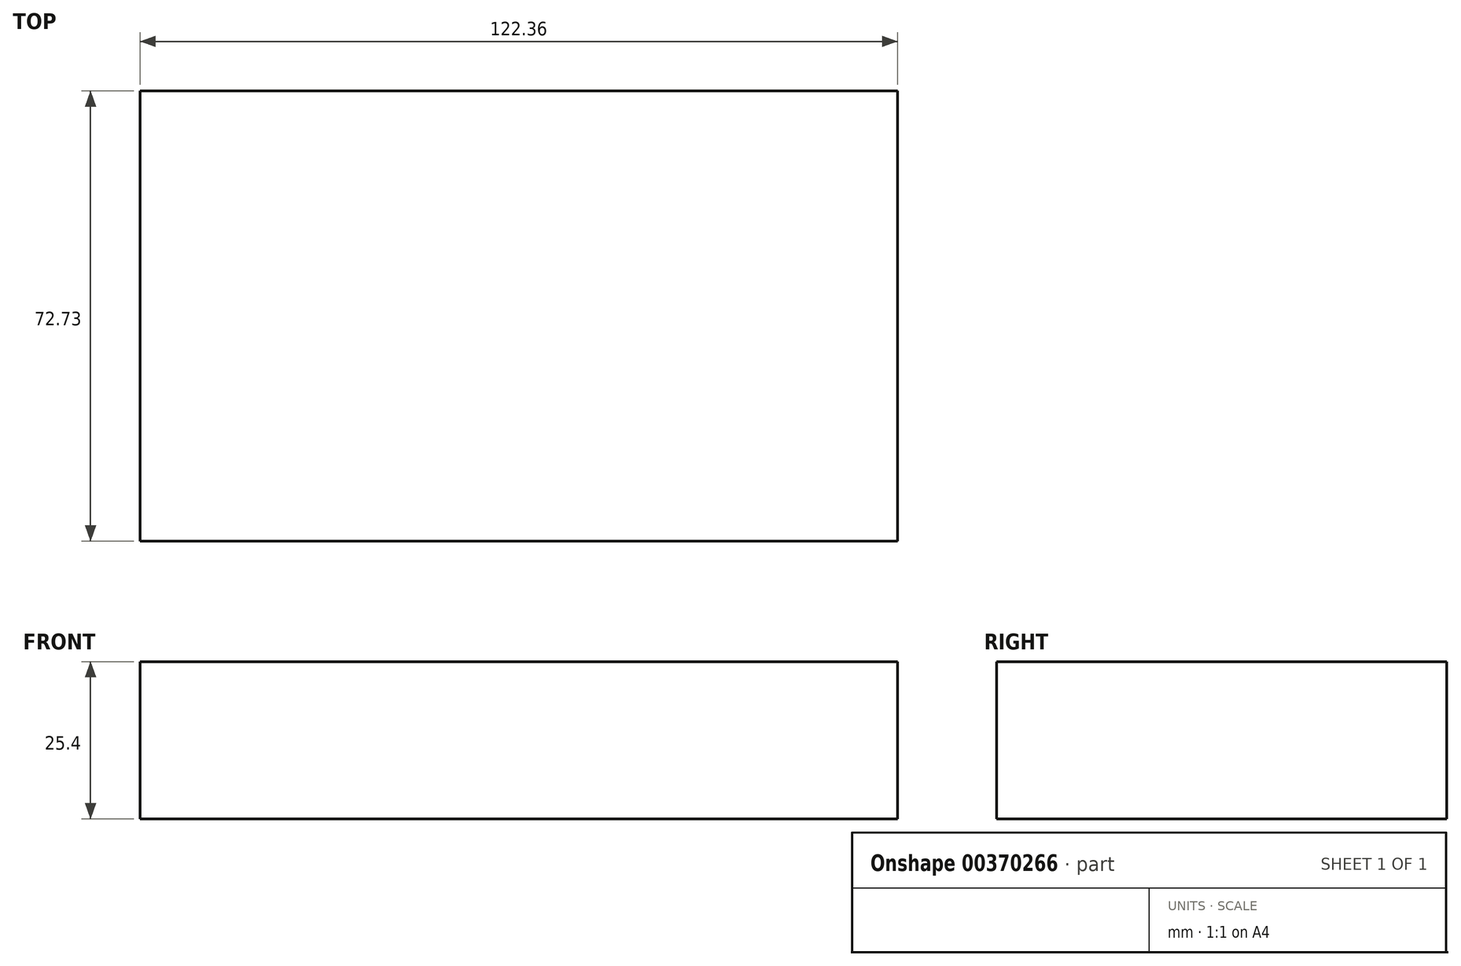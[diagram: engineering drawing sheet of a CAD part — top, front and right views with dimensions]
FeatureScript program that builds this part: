
annotation { "Feature Type Name" : "Feature", "Feature Type Description" : "" }
export const myFeature = defineFeature(function(context is Context, id is Id, definition is map)
    precondition{}
    {
        {
            var Q0;
            Q0=qCreatedBy(makeId("Top.planeOp"),FACE);
            var sketch = newSketch(context, id + "F0", { "sketchPlane" : qUnion([Q0])});
            skLineSegment(sketch, "E0.bottom", {"start": v(-61.18, -72.73) * mm, "end": v(61.18, -72.73) * mm});
            skLineSegment(sketch, "E0.top", {"start": v(-61.18, 0) * mm, "end": v(61.18, 0) * mm});
            skLineSegment(sketch, "E0.left", {"start": v(-61.18, -72.73) * mm, "end": v(-61.18, 0) * mm});
            skLineSegment(sketch, "E0.right", {"start": v(61.18, -72.73) * mm, "end": v(61.18, 0) * mm});
            skSolve(sketch);
        }
        {
            var Q0;
            Q0=makeQuery(id+"F0.imprint","IMPRINT",FACE,{"disambiguationData":[TD([[makeQuery(id+"F0.imprint","IMPRINT",EDGE,{"derivedFrom":sQuery(id+"F0.wireOp",EDGE,"E0.bottom")}),1.0]])]});
            extrude(context, id + "F1", {"entities" : qUnion([Q0]), "depth" : 25.4 * mm, "offsetDistance" : 25.4 * mm});
        }
    });
